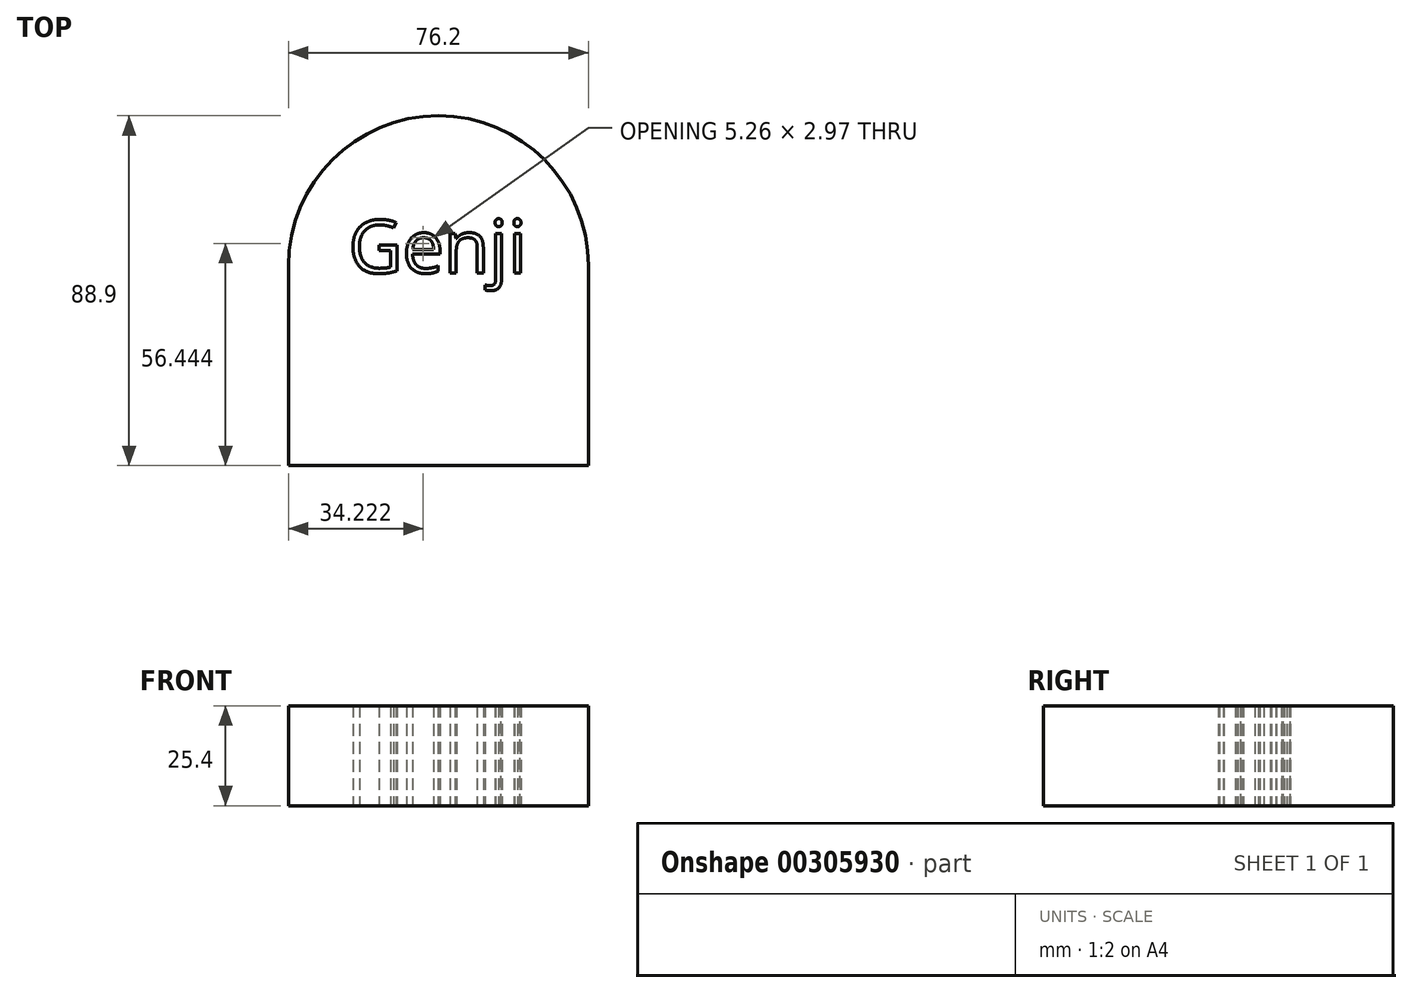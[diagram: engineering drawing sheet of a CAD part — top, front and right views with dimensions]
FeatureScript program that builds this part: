
annotation { "Feature Type Name" : "Feature", "Feature Type Description" : "" }
export const myFeature = defineFeature(function(context is Context, id is Id, definition is map)
    precondition{}
    {
        {
            var Q0;
            Q0=qCreatedBy(makeId("Top.planeOp"),FACE);
            var sketch = newSketch(context, id + "F0", { "sketchPlane" : qUnion([Q0])});
            skLineSegment(sketch, "E0", {"start": v(-50.13, -30) * mm, "end": v(26.07, -30) * mm});
            skLineSegment(sketch, "E1", {"start": v(26.07, -30) * mm, "end": v(26.07, 20.8) * mm});
            skLineSegment(sketch, "E2", {"start": v(-50.13, -30) * mm, "end": v(-50.13, 20.8) * mm});
            skArc(sketch, "E3", {"start": v(26.07, 20.8) * mm, "mid": v(-12.03, 58.9) * mm, "end": v(-50.13, 20.8) * mm});
            skSolve(sketch);
        }
        {
            var Q0;
            Q0 = qSketchRegion(id + "F0", true);
            extrude(context, id + "F1", {"entities" : qUnion([Q0]), "depth" : 25.4 * mm});
        }
        {
            var Q0;
            Q0=qCreatedBy(makeId("Top.planeOp"),FACE);
            var sketch = newSketch(context, id + "F2", { "sketchPlane" : qUnion([Q0])});
            skText(sketch, "E4", { "text": "Genji\n", "fontName": "OpenSans-Regular.ttf"});
            const initialGuessF2  = {"E4": [-0.0349, 0.01895, 1, 0, 0.01354]};
            skSetInitialGuess(sketch, initialGuessF2);
            skSolve(sketch);
        }
        {
            var Q0;
            Q0 = qSketchRegion(id + "F2", true);
            var Q1;
            Q1 = qConstructionFilter(qBodyType(qCreatedBy(id + "F2" ,EDGE), BodyType.WIRE), ConstructionObject.NO);
            extrude(context, id + "F3", {"entities" : qUnion([Q0]), "surfaceEntities" : qUnion([Q1]), "depth" : 25.4 * mm});
        }
    });
